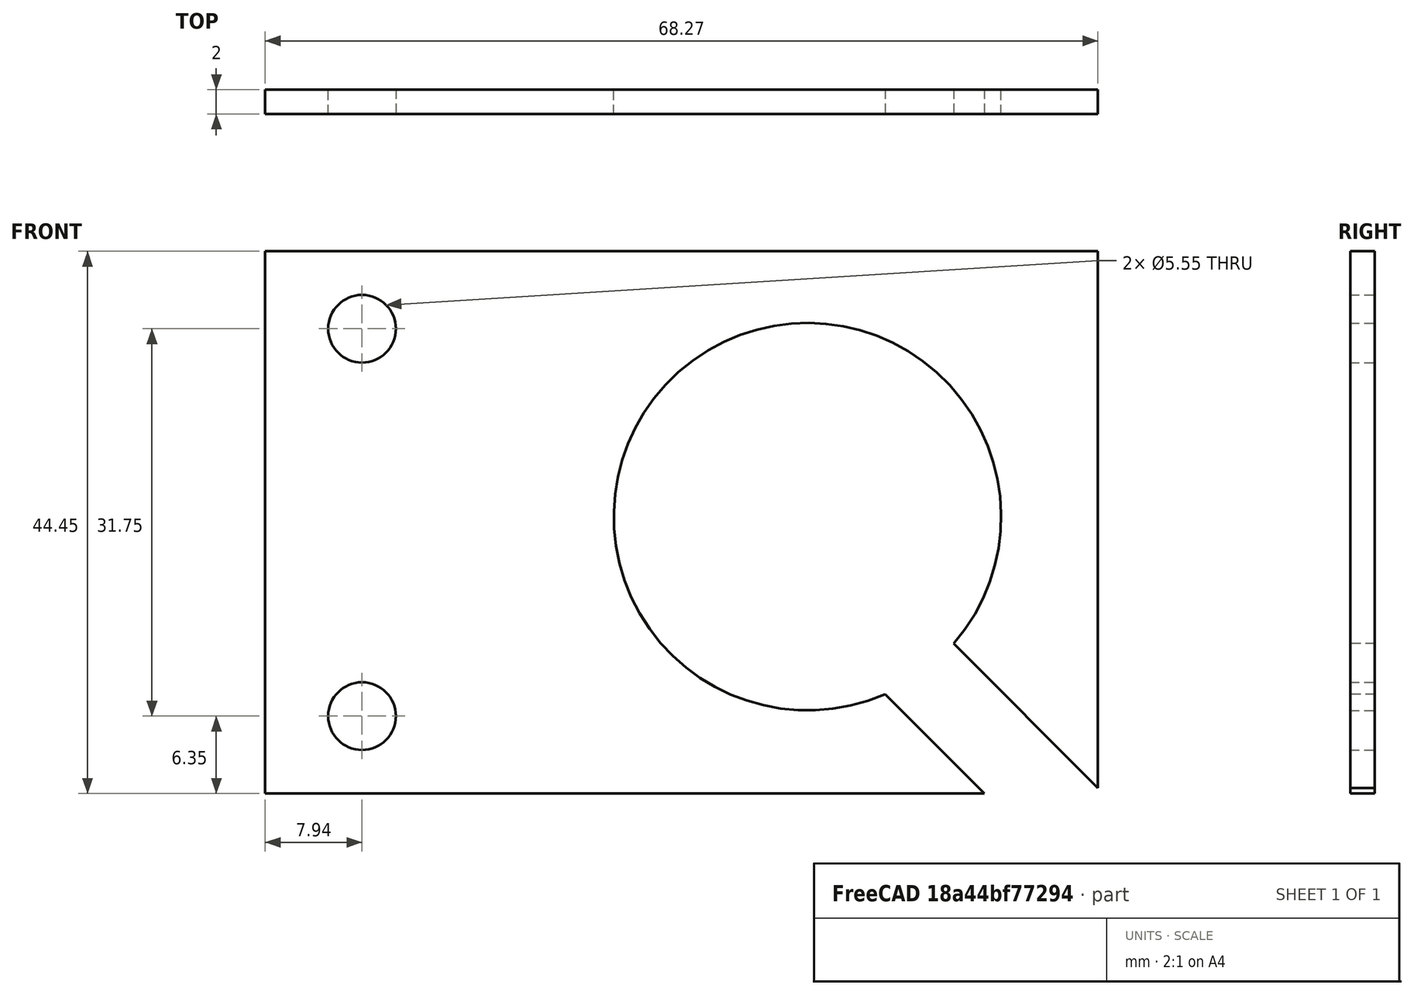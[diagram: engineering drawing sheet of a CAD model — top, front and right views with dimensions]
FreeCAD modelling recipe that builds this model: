
FCSTD DOCUMENT  (FreeCAD 0.19R14555 (Git shallow))
Label: 1U_CableGuide_v0
License: All rights reserved
LicenseURL: http://en.wikipedia.org/wiki/All_rights_reserved
objects: Sketcher::SketchObject×1, PartDesign::Pad×1, PartDesign::Body×1
note: 4 computed .brp shape members not serialized (recipe doc carries the construction recipe); baked Part::Feature solids carry a one-line shape summary decoded from their .brp

FEATURE [Sketcher::SketchObject] Sketch
  FullyConstrained = false
  MapMode = 5
  Placement = pos=(0,0,0) rot=(1,0,0;1.5708rad)
  Support = -> [XZ_Plane]
  expr: Constraints[18] = 31.75 / 2 + 6.35
  expr: Constraints[17] = 31.75 / 2 + 7.94
  expr: Constraints[16] = 44.45 - 6.35 * 2
  expr: Constraints[15] = 44.45 + 7.94 * 2
  sketch-geometry (9):
    g0: LineSegment StartX=0 StartY=0 StartZ=0 EndX=58.9564 EndY=0 EndZ=0
    g1: LineSegment StartX=68.27 StartY=0.472633 StartZ=0 EndX=68.27 EndY=44.45 EndZ=0
    g2: LineSegment StartX=68.27 StartY=44.45 StartZ=0 EndX=0 EndY=44.45 EndZ=0
    g3: LineSegment StartX=0 StartY=44.45 StartZ=0 EndX=0 EndY=0 EndZ=0
    g4: Circle CenterX=7.94 CenterY=6.35 CenterZ=0 NormalX=0 NormalY=0 NormalZ=1 AngleXU=0 Radius=2.775
    g5: Circle CenterX=7.94 CenterY=38.1 CenterZ=0 NormalX=0 NormalY=0 NormalZ=1 AngleXU=0 Radius=2.775
    g6: ArcOfCircle CenterX=44.455 CenterY=22.6976 CenterZ=0 NormalX=0 NormalY=0 NormalZ=1 AngleXU=0 Radius=15.875 StartAngle=5.56867 EndAngle=11.4073
    g7: LineSegment StartX=68.27 StartY=0.472633 StartZ=0 EndX=56.4471 EndY=12.2955 EndZ=0
    g8: LineSegment StartX=58.9564 StartY=0 StartZ=0 EndX=50.8074 EndY=8.149 EndZ=0
  constraints (26):
    c: Coincident(g1,g2)
    c: Coincident(g2,g3)
    c: Coincident(g3,g0)
    c: Horizontal(g0)
    c: Horizontal(g2)
    c: Vertical(g1)
    c: Vertical(g3)
    c: Coincident(g0,g-1)
    c: DistanceY(g3,g3) = 44.45
    c: Diameter(g4) = 5.55
    c: DistanceX(g0,g4) = 7.94
    c: DistanceY(g0,g4) = 6.35
    c: Equal(g4,g5) = 5.55
    c: Vertical(g5,g4)
    c: DistanceY(g5,g2) = 6.35
    c: DistanceX(g4,g1) = 60.33
    c: Diameter(g6) = 31.75
    c: DistanceX(g6,g1) = 23.815
    c: DistanceY(g1,g6) = 22.225
    c: Coincident(g7,g1)
    c: Angle(g7,g0) = 0.785398
    c: Angle(g8,g0) = 0.785398
    c: Distance(g7,g8) = 7
    c: Coincident(g6,g7)
    c: Coincident(g6,g8)
    c: Coincident(g0,g8)
FEATURE [PartDesign::Pad] Pad
  Direction = (1,1,1)
  Length = 2
  Length2 = 100
  Placement = pos=(0,0,0) rot=(1,0,0;1.5708rad)
  Profile = -> Sketch
  Type = 0
FEATURE [PartDesign::Body] Body
  Group = -> [Sketch,Pad]
  Origin = -> Origin
  Tip = -> Pad
